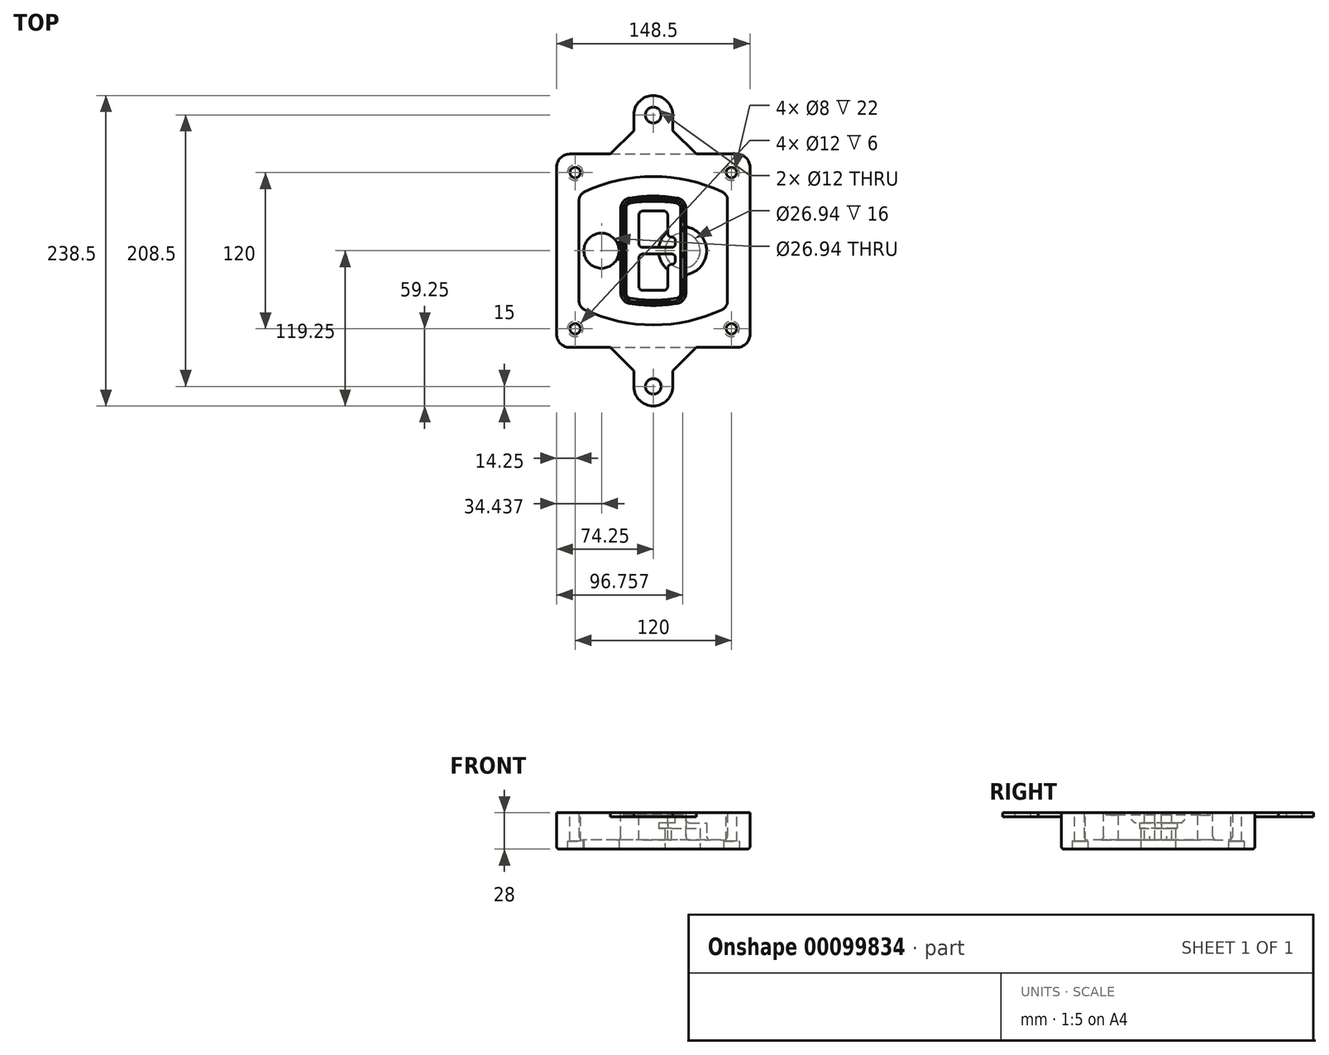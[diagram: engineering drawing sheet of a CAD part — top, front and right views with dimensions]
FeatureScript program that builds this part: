
annotation { "Feature Type Name" : "Feature", "Feature Type Description" : "" }
export const myFeature = defineFeature(function(context is Context, id is Id, definition is map)
    precondition{}
    {
        {
            var Q0;
            Q0=qCreatedBy(makeId("Top.planeOp"),FACE);
            var sketch = newSketch(context, id + "F0", { "sketchPlane" : qUnion([Q0])});
            skPoint(sketch, "E0.rect.middle", {"position": v(0, 0) * mm});
            skLineSegment(sketch, "E1.bottom", {"start": v(-64.25, -74.25) * mm, "end": v(64.25, -74.25) * mm});
            skLineSegment(sketch, "E1.top", {"start": v(-64.25, 74.25) * mm, "end": v(64.25, 74.25) * mm});
            skLineSegment(sketch, "E1.left", {"start": v(-74.25, -64.25) * mm, "end": v(-74.25, 64.25) * mm});
            skLineSegment(sketch, "E1.right", {"start": v(74.25, -64.25) * mm, "end": v(74.25, 64.25) * mm});
            skLineSegment(sketch, "E2", {"start": v(-74.25, 74.25) * mm, "end": v(74.25, -74.25) * mm, "construction": true});
            skLineSegment(sketch, "E3", {"start": v(74.25, 74.25) * mm, "end": v(-74.25, -74.25) * mm, "construction": true});
            skCircle(sketch, "E4", {"center": v(-60, 60) * mm, "radius": 4 * mm});
            skCircle(sketch, "E5", {"center": v(60, 60) * mm, "radius": 4 * mm});
            skCircle(sketch, "E6", {"center": v(60, -60) * mm, "radius": 4 * mm});
            skCircle(sketch, "E7", {"center": v(-60, -60) * mm, "radius": 4 * mm});
            skLineSegment(sketch, "E8", {"start": v(-60, 60) * mm, "end": v(60, 60) * mm, "construction": true});
            skLineSegment(sketch, "E9", {"start": v(60, 60) * mm, "end": v(60, -60) * mm, "construction": true});
            skLineSegment(sketch, "E10", {"start": v(60, -60) * mm, "end": v(-60, -60) * mm, "construction": true});
            skLineSegment(sketch, "E11", {"start": v(-60, -60) * mm, "end": v(-60, 60) * mm, "construction": true});
            skLineSegment(sketch, "E12", {"start": v(-60, 38.83) * mm, "end": v(-60, -38.83) * mm});
            skLineSegment(sketch, "E13", {"start": v(60, 38.83) * mm, "end": v(60, -38.83) * mm});
            skArc(sketch, "E14", {"start": v(54.26, 47.88) * mm, "mid": v(0, 60) * mm, "end": v(-54.26, 47.88) * mm});
            skArc(sketch, "E15", {"start": v(-54.26, -47.88) * mm, "mid": v(0, -60) * mm, "end": v(54.26, -47.88) * mm});
            skLineSegment(sketch, "E16", {"start": v(-60, 0) * mm, "end": v(60, 0) * mm, "construction": true});
            skPoint(sketch, "E17.visualSharp", {"position": v(-60, -45) * mm});
            skArc(sketch, "E17.filletArc", {"start": v(-60, -38.83) * mm, "mid": v(-58.44, -44.2) * mm, "end": v(-54.26, -47.88) * mm});
            skPoint(sketch, "E18.visualSharp", {"position": v(-60, 45) * mm});
            skArc(sketch, "E18.filletArc", {"start": v(-54.26, 47.88) * mm, "mid": v(-58.44, 44.2) * mm, "end": v(-60, 38.83) * mm});
            skPoint(sketch, "E19.visualSharp", {"position": v(60, 45) * mm});
            skArc(sketch, "E19.filletArc", {"start": v(60, 38.83) * mm, "mid": v(58.44, 44.2) * mm, "end": v(54.26, 47.88) * mm});
            skPoint(sketch, "E20.visualSharp", {"position": v(60, -45) * mm});
            skArc(sketch, "E20.filletArc", {"start": v(54.26, -47.88) * mm, "mid": v(58.44, -44.2) * mm, "end": v(60, -38.83) * mm});
            skPoint(sketch, "E21.visualSharp", {"position": v(-74.25, 74.25) * mm});
            skArc(sketch, "E21.filletArc", {"start": v(-64.25, 74.25) * mm, "mid": v(-71.32, 71.32) * mm, "end": v(-74.25, 64.25) * mm});
            skPoint(sketch, "E22.visualSharp", {"position": v(74.25, 74.25) * mm});
            skArc(sketch, "E22.filletArc", {"start": v(74.25, 64.25) * mm, "mid": v(71.32, 71.32) * mm, "end": v(64.25, 74.25) * mm});
            skPoint(sketch, "E23.visualSharp", {"position": v(74.25, -74.25) * mm});
            skArc(sketch, "E23.filletArc", {"start": v(64.25, -74.25) * mm, "mid": v(71.32, -71.32) * mm, "end": v(74.25, -64.25) * mm});
            skPoint(sketch, "E24.visualSharp", {"position": v(-74.25, -74.25) * mm});
            skArc(sketch, "E24.filletArc", {"start": v(-74.25, -64.25) * mm, "mid": v(-71.32, -71.32) * mm, "end": v(-64.25, -74.25) * mm});
            skArc(sketch, "E25.0", {"start": v(57, 38.83) * mm, "mid": v(55.9, 42.58) * mm, "end": v(52.98, 45.17) * mm});
            skLineSegment(sketch, "E25.1", {"start": v(57, 38.83) * mm, "end": v(57, -38.83) * mm});
            skArc(sketch, "E25.2", {"start": v(52.98, -45.17) * mm, "mid": v(55.9, -42.58) * mm, "end": v(57, -38.83) * mm});
            skArc(sketch, "E25.3", {"start": v(-52.98, -45.17) * mm, "mid": v(0, -57) * mm, "end": v(52.98, -45.17) * mm});
            skArc(sketch, "E25.4", {"start": v(-57, -38.83) * mm, "mid": v(-55.9, -42.58) * mm, "end": v(-52.98, -45.17) * mm});
            skArc(sketch, "E25.5", {"start": v(52.98, 45.17) * mm, "mid": v(0, 57) * mm, "end": v(-52.98, 45.17) * mm});
            skLineSegment(sketch, "E25.6", {"start": v(-57, 38.83) * mm, "end": v(-57, -38.83) * mm});
            skArc(sketch, "E25.7", {"start": v(-52.98, 45.17) * mm, "mid": v(-55.9, 42.58) * mm, "end": v(-57, 38.83) * mm});
            skArc(sketch, "E26.0", {"start": v(-55.96, 51.5) * mm, "mid": v(-61.82, 46.33) * mm, "end": v(-64, 38.83) * mm});
            skArc(sketch, "E26.1", {"start": v(55.96, 51.5) * mm, "mid": v(0, 64) * mm, "end": v(-55.96, 51.5) * mm});
            skArc(sketch, "E26.2", {"start": v(64, 38.83) * mm, "mid": v(61.82, 46.33) * mm, "end": v(55.96, 51.5) * mm});
            skLineSegment(sketch, "E26.3", {"start": v(64, 38.83) * mm, "end": v(64, -38.83) * mm});
            skArc(sketch, "E26.4", {"start": v(55.96, -51.5) * mm, "mid": v(61.82, -46.33) * mm, "end": v(64, -38.83) * mm});
            skLineSegment(sketch, "E26.5", {"start": v(-64, 38.83) * mm, "end": v(-64, -38.83) * mm});
            skArc(sketch, "E26.6", {"start": v(-55.96, -51.5) * mm, "mid": v(0, -64) * mm, "end": v(55.96, -51.5) * mm});
            skArc(sketch, "E26.7", {"start": v(-64, -38.83) * mm, "mid": v(-61.82, -46.33) * mm, "end": v(-55.96, -51.5) * mm});
            skSolve(sketch);
        }
        {
            var Q0;
            Q0=makeQuery(id+"F0.imprint","IMPRINT",FACE,{"disambiguationData":[TD([[makeQuery(id+"F0.imprint","IMPRINT",EDGE,{"derivedFrom":sQuery(id+"F0.wireOp",EDGE,"E1.bottom")}),1.0]])]});
            var Q1;
            Q1=makeQuery(id+"F0.imprint","IMPRINT",FACE,{"disambiguationData":[TD([[makeQuery(id+"F0.imprint","IMPRINT",EDGE,{"derivedFrom":sQuery(id+"F0.wireOp",EDGE,"E12")}),1.0]])]});
            var Q2;
            Q2=makeQuery(id+"F0.imprint","IMPRINT",FACE,{"disambiguationData":[TD([[makeQuery(id+"F0.imprint","IMPRINT",EDGE,{"derivedFrom":sQuery(id+"F0.wireOp",EDGE,"E25.0")}),1.0]])]});
            var Q3;
            Q3=makeQuery(id+"F0.imprint","IMPRINT",FACE,{"disambiguationData":[TD([[makeQuery(id+"F0.imprint","IMPRINT",EDGE,{"derivedFrom":sQuery(id+"F0.wireOp",EDGE,"E12")}),-1.0]])]});
            extrude(context, id + "F1", {"entities" : qUnion([Q0, Q1, Q2, Q3]), "oppositeDirection" : true, "depth" : 25 * mm});
        }
        {
            var Q0;
            Q0=makeQuery(id+"F0.imprint","IMPRINT",FACE,{"disambiguationData":[TD([[makeQuery(id+"F0.imprint","IMPRINT",EDGE,{"derivedFrom":sQuery(id+"F0.wireOp",EDGE,"E12")}),1.0]])]});
            extrude(context, id + "F2", {"entities" : qUnion([Q0]), "operationType" : NewBodyOperationType.ADD, "depth" : 3 * mm});
        }
        {
            var Q0;
            Q0=makeQuery(id+"F0.imprint","IMPRINT",FACE,{"disambiguationData":[TD([[makeQuery(id+"F0.imprint","IMPRINT",EDGE,{"derivedFrom":sQuery(id+"F0.wireOp",EDGE,"E25.0")}),1.0]])]});
            extrude(context, id + "F3", {"entities" : qUnion([Q0]), "operationType" : NewBodyOperationType.REMOVE, "oppositeDirection" : true, "depth" : 18 * mm});
        }
        {
            var Q0;
            Q0=makeQuery(id+"F2.opExtrude","CAP_FACE",FACE,{"disambiguationData":[OSD([sQuery(id+"F0.wireOp",EDGE,"E12"),sQuery(id+"F0.wireOp",EDGE,"E13"),sQuery(id+"F0.wireOp",EDGE,"E14"),sQuery(id+"F0.wireOp",EDGE,"E15"),sQuery(id+"F0.wireOp",EDGE,"E17.filletArc"),sQuery(id+"F0.wireOp",EDGE,"E18.filletArc"),sQuery(id+"F0.wireOp",EDGE,"E19.filletArc"),sQuery(id+"F0.wireOp",EDGE,"E20.filletArc"),sQuery(id+"F0.wireOp",EDGE,"E25.0"),sQuery(id+"F0.wireOp",EDGE,"E25.1"),sQuery(id+"F0.wireOp",EDGE,"E25.2"),sQuery(id+"F0.wireOp",EDGE,"E25.3"),sQuery(id+"F0.wireOp",EDGE,"E25.4"),sQuery(id+"F0.wireOp",EDGE,"E25.5"),sQuery(id+"F0.wireOp",EDGE,"E25.6"),sQuery(id+"F0.wireOp",EDGE,"E25.7")])],"isStart":false});
            var sketch = newSketch(context, id + "F4", { "sketchPlane" : qUnion([Q0])});
            skArc(sketch, "E27.0", {"start": v(-18.34, -40.45) * mm, "mid": v(0, -42) * mm, "end": v(18.34, -40.45) * mm});
            skArc(sketch, "E28.0", {"start": v(18.34, 40.45) * mm, "mid": v(0, 42) * mm, "end": v(-18.34, 40.45) * mm});
            skLineSegment(sketch, "E29", {"start": v(-25, 32.57) * mm, "end": v(-25, -32.57) * mm});
            skLineSegment(sketch, "E30", {"start": v(25, 32.57) * mm, "end": v(25, -32.57) * mm});
            skLineSegment(sketch, "E31", {"start": v(-25, 39.1) * mm, "end": v(25, 39.1) * mm, "construction": true});
            skLineSegment(sketch, "E32", {"start": v(-25, -39.1) * mm, "end": v(25, -39.1) * mm, "construction": true});
            skPoint(sketch, "E33.visualSharp", {"position": v(-25, 39.1) * mm});
            skArc(sketch, "E33.filletArc", {"start": v(-18.34, 40.45) * mm, "mid": v(-23.11, 37.73) * mm, "end": v(-25, 32.57) * mm});
            skPoint(sketch, "E34.visualSharp", {"position": v(25, 39.1) * mm});
            skArc(sketch, "E34.filletArc", {"start": v(25, 32.57) * mm, "mid": v(23.11, 37.73) * mm, "end": v(18.34, 40.45) * mm});
            skPoint(sketch, "E35.visualSharp", {"position": v(25, -39.1) * mm});
            skArc(sketch, "E35.filletArc", {"start": v(18.34, -40.45) * mm, "mid": v(23.11, -37.73) * mm, "end": v(25, -32.57) * mm});
            skPoint(sketch, "E36.visualSharp", {"position": v(-25, -39.1) * mm});
            skArc(sketch, "E36.filletArc", {"start": v(-25, -32.57) * mm, "mid": v(-23.11, -37.73) * mm, "end": v(-18.34, -40.45) * mm});
            skArc(sketch, "E37.0", {"start": v(52.98, 45.17) * mm, "mid": v(0, 57) * mm, "end": v(-52.98, 45.17) * mm});
            skArc(sketch, "E37.1", {"start": v(-52.98, 45.17) * mm, "mid": v(-55.9, 42.58) * mm, "end": v(-57, 38.83) * mm});
            skLineSegment(sketch, "E37.2", {"start": v(-57, 38.83) * mm, "end": v(-57, -38.83) * mm});
            skArc(sketch, "E37.3", {"start": v(-57, -38.83) * mm, "mid": v(-55.9, -42.58) * mm, "end": v(-52.98, -45.17) * mm});
            skArc(sketch, "E37.4", {"start": v(-52.98, -45.17) * mm, "mid": v(0, -57) * mm, "end": v(52.98, -45.17) * mm});
            skArc(sketch, "E37.5", {"start": v(52.98, -45.17) * mm, "mid": v(55.9, -42.58) * mm, "end": v(57, -38.83) * mm});
            skLineSegment(sketch, "E37.6", {"start": v(57, 38.83) * mm, "end": v(57, -38.83) * mm});
            skArc(sketch, "E37.7", {"start": v(57, 38.83) * mm, "mid": v(55.9, 42.58) * mm, "end": v(52.98, 45.17) * mm});
            skLineSegment(sketch, "E38.0", {"start": v(23, 32.57) * mm, "end": v(23, -32.57) * mm});
            skArc(sketch, "E38.1", {"start": v(18, -38.48) * mm, "mid": v(21.58, -36.44) * mm, "end": v(23, -32.57) * mm});
            skArc(sketch, "E38.2", {"start": v(-18, -38.48) * mm, "mid": v(0, -40) * mm, "end": v(18, -38.48) * mm});
            skArc(sketch, "E38.3", {"start": v(-23, -32.57) * mm, "mid": v(-21.58, -36.44) * mm, "end": v(-18, -38.48) * mm});
            skLineSegment(sketch, "E38.4", {"start": v(-23, 32.57) * mm, "end": v(-23, -32.57) * mm});
            skArc(sketch, "E38.5", {"start": v(23, 32.57) * mm, "mid": v(21.58, 36.44) * mm, "end": v(18, 38.48) * mm});
            skArc(sketch, "E38.6", {"start": v(-18, 38.48) * mm, "mid": v(-21.58, 36.44) * mm, "end": v(-23, 32.57) * mm});
            skArc(sketch, "E38.7", {"start": v(18, 38.48) * mm, "mid": v(0, 40) * mm, "end": v(-18, 38.48) * mm});
            skArc(sketch, "E39.0", {"start": v(21, 32.57) * mm, "mid": v(20.06, 35.15) * mm, "end": v(17.67, 36.5) * mm});
            skLineSegment(sketch, "E39.1", {"start": v(21, 32.57) * mm, "end": v(21, -32.57) * mm});
            skArc(sketch, "E39.2", {"start": v(17.67, -36.5) * mm, "mid": v(20.06, -35.15) * mm, "end": v(21, -32.57) * mm});
            skArc(sketch, "E39.3", {"start": v(-17.67, -36.5) * mm, "mid": v(0, -38) * mm, "end": v(17.67, -36.5) * mm});
            skArc(sketch, "E39.4", {"start": v(-21, -32.57) * mm, "mid": v(-20.06, -35.15) * mm, "end": v(-17.67, -36.5) * mm});
            skArc(sketch, "E39.5", {"start": v(17.67, 36.5) * mm, "mid": v(0, 38) * mm, "end": v(-17.67, 36.5) * mm});
            skLineSegment(sketch, "E39.6", {"start": v(-21, 32.57) * mm, "end": v(-21, -32.57) * mm});
            skArc(sketch, "E39.7", {"start": v(-17.67, 36.5) * mm, "mid": v(-20.06, 35.15) * mm, "end": v(-21, 32.57) * mm});
            skLineSegment(sketch, "E40", {"start": v(-25, 0) * mm, "end": v(25, 0) * mm, "construction": true});
            skLineSegment(sketch, "E41", {"start": v(-11, 5.5) * mm, "end": v(-11, 27.5) * mm});
            skLineSegment(sketch, "E42", {"start": v(-8, 30.5) * mm, "end": v(8, 30.5) * mm});
            skLineSegment(sketch, "E43", {"start": v(11, 27.5) * mm, "end": v(11, 13.5) * mm});
            skLineSegment(sketch, "E44", {"start": v(14, 10.5) * mm, "end": v(14, 10.5) * mm});
            skLineSegment(sketch, "E45", {"start": v(17, 7.5) * mm, "end": v(17, 5.5) * mm});
            skLineSegment(sketch, "E46", {"start": v(14, 2.5) * mm, "end": v(-8, 2.5) * mm});
            skPoint(sketch, "E47.visualSharp", {"position": v(-11, 30.5) * mm});
            skArc(sketch, "E47.filletArc", {"start": v(-8, 30.5) * mm, "mid": v(-10.12, 29.62) * mm, "end": v(-11, 27.5) * mm});
            skPoint(sketch, "E48.visualSharp", {"position": v(11, 30.5) * mm});
            skArc(sketch, "E48.filletArc", {"start": v(11, 27.5) * mm, "mid": v(10.12, 29.62) * mm, "end": v(8, 30.5) * mm});
            skPoint(sketch, "E49.visualSharp", {"position": v(11, 10.5) * mm});
            skArc(sketch, "E49.filletArc", {"start": v(11, 13.5) * mm, "mid": v(11.88, 11.38) * mm, "end": v(14, 10.5) * mm});
            skPoint(sketch, "E50.visualSharp", {"position": v(17, 10.5) * mm});
            skArc(sketch, "E50.filletArc", {"start": v(17, 7.5) * mm, "mid": v(16.12, 9.62) * mm, "end": v(14, 10.5) * mm});
            skPoint(sketch, "E51.visualSharp", {"position": v(17, 2.5) * mm});
            skArc(sketch, "E51.filletArc", {"start": v(14, 2.5) * mm, "mid": v(16.12, 3.38) * mm, "end": v(17, 5.5) * mm});
            skPoint(sketch, "E52.visualSharp", {"position": v(-11, 2.5) * mm});
            skArc(sketch, "E52.filletArc", {"start": v(-11, 5.5) * mm, "mid": v(-10.12, 3.38) * mm, "end": v(-8, 2.5) * mm});
            skLineSegment(sketch, "E53.0.MirrorCS", {"start": v(14, -2.5) * mm, "end": v(-8, -2.5) * mm});
            skArc(sketch, "E54.0.MirrorCS", {"start": v(-11, -5.5) * mm, "mid": v(-10.12, -3.38) * mm, "end": v(-8, -2.5) * mm});
            skLineSegment(sketch, "E55.0.MirrorCS", {"start": v(-11, -5.5) * mm, "end": v(-11, -27.5) * mm});
            skArc(sketch, "E56.0.MirrorCS", {"start": v(-8, -30.5) * mm, "mid": v(-10.12, -29.62) * mm, "end": v(-11, -27.5) * mm});
            skLineSegment(sketch, "E57.0.MirrorCS", {"start": v(-8, -30.5) * mm, "end": v(8, -30.5) * mm});
            skArc(sketch, "E58.0.MirrorCS", {"start": v(11, -27.5) * mm, "mid": v(10.12, -29.62) * mm, "end": v(8, -30.5) * mm});
            skLineSegment(sketch, "E59.0.MirrorCS", {"start": v(11, -27.5) * mm, "end": v(11, -13.5) * mm});
            skArc(sketch, "E60.0.MirrorCS", {"start": v(11, -13.5) * mm, "mid": v(11.88, -11.38) * mm, "end": v(14, -10.5) * mm});
            skArc(sketch, "E61.0.MirrorCS", {"start": v(17, -7.5) * mm, "mid": v(16.12, -9.62) * mm, "end": v(14, -10.5) * mm});
            skLineSegment(sketch, "E62.0.MirrorCS", {"start": v(17, -7.5) * mm, "end": v(17, -5.5) * mm});
            skArc(sketch, "E63.0.MirrorCS", {"start": v(14, -2.5) * mm, "mid": v(16.12, -3.38) * mm, "end": v(17, -5.5) * mm});
            skSolve(sketch);
        }
        {
            var Q0;
            Q0=makeQuery(id+"F4.imprint","IMPRINT",FACE,{"disambiguationData":[TD([[makeQuery(id+"F4.imprint","IMPRINT",EDGE,{"derivedFrom":sQuery(id+"F4.wireOp",EDGE,"E27.0")}),1.0]])]});
            var Q1;
            Q1=makeQuery(id+"F4.imprint","IMPRINT",FACE,{"disambiguationData":[TD([[makeQuery(id+"F4.imprint","IMPRINT",EDGE,{"derivedFrom":sQuery(id+"F4.wireOp",EDGE,"E38.0")}),-1.0]])]});
            var Q2;
            Q2=makeQuery(id+"F4.imprint","IMPRINT",FACE,{"disambiguationData":[TD([[makeQuery(id+"F4.imprint","IMPRINT",EDGE,{"derivedFrom":sQuery(id+"F4.wireOp",EDGE,"E39.0")}),1.0]])]});
            extrude(context, id + "F5", {"entities" : qUnion([Q0, Q1, Q2]), "operationType" : NewBodyOperationType.ADD, "endBound" : BoundingType.UP_TO_NEXT, "oppositeDirection" : true, "depth" : 25 * mm});
        }
        {
            var Q0;
            Q0=makeQuery(id+"F4.imprint","IMPRINT",FACE,{"disambiguationData":[TD([[makeQuery(id+"F4.imprint","IMPRINT",EDGE,{"derivedFrom":sQuery(id+"F4.wireOp",EDGE,"E38.0")}),-1.0]])]});
            extrude(context, id + "F6", {"entities" : qUnion([Q0]), "operationType" : NewBodyOperationType.REMOVE, "oppositeDirection" : true, "depth" : 2 * mm});
        }
        {
            var Q0;
            Q0=makeQuery(id+"F1.opExtrude","CAP_FACE",FACE,{"disambiguationData":[OSD([sQuery(id+"F0.wireOp",EDGE,"E1.bottom"),sQuery(id+"F0.wireOp",EDGE,"E1.top"),sQuery(id+"F0.wireOp",EDGE,"E1.left"),sQuery(id+"F0.wireOp",EDGE,"E1.right"),sQuery(id+"F0.wireOp",EDGE,"E4"),sQuery(id+"F0.wireOp",EDGE,"E5"),sQuery(id+"F0.wireOp",EDGE,"E6"),sQuery(id+"F0.wireOp",EDGE,"E7"),sQuery(id+"F0.wireOp",EDGE,"E21.filletArc"),sQuery(id+"F0.wireOp",EDGE,"E22.filletArc"),sQuery(id+"F0.wireOp",EDGE,"E23.filletArc"),sQuery(id+"F0.wireOp",EDGE,"E24.filletArc")])],"isStart":false});
            var sketch = newSketch(context, id + "F7", { "sketchPlane" : qUnion([Q0])});
            skCircle(sketch, "E64", {"center": v(22.5, 0) * mm, "radius": 13.47 * mm});
            skCircle(sketch, "E65", {"center": v(-39.81, 0) * mm, "radius": 13.47 * mm});
            skLineSegment(sketch, "E66", {"start": v(74.25, 0) * mm, "end": v(-74.25, 0) * mm});
            skCircle(sketch, "E67", {"center": v(22.5, 0) * mm, "radius": 18.47 * mm});
            skCircle(sketch, "E68", {"center": v(60, -60) * mm, "radius": 6 * mm});
            skCircle(sketch, "E69", {"center": v(-60, -60) * mm, "radius": 6 * mm});
            skCircle(sketch, "E70", {"center": v(-60, 60) * mm, "radius": 6 * mm});
            skCircle(sketch, "E71", {"center": v(60, 60) * mm, "radius": 6 * mm});
            skSolve(sketch);
        }
        {
            var Q0;
            {var subQ1=sQuery(id+"F7.wireOp",EDGE,"E66");var subQ4=sQuery(id+"F7.wireOp",EDGE,"E64");var subQ6=makeQuery(id+"F7.imprint","INTERSECT",VERTEX,{"disambiguationData":[OD(0.0)],"derivedFrom":[subQ4,subQ1]});Q0=makeQuery(id+"F7.imprint","IMPRINT",FACE,{"disambiguationData":[TD([[makeQuery(id+"F7.imprint","IMPRINT",EDGE,{"disambiguationData":[TD([[subQ6,-1.0]])],"derivedFrom":subQ4}),-1.0]])]});}
            var Q1;
            {var subQ0=sQuery(id+"F7.wireOp",EDGE,"E66");var subQ1=sQuery(id+"F7.wireOp",EDGE,"E64");var subQ3=makeQuery(id+"F7.imprint","INTERSECT",VERTEX,{"disambiguationData":[OD(0.0)],"derivedFrom":[subQ1,subQ0]});Q1=makeQuery(id+"F7.imprint","IMPRINT",FACE,{"disambiguationData":[TD([[makeQuery(id+"F7.imprint","IMPRINT",EDGE,{"disambiguationData":[TD([[subQ3,-1.0]])],"derivedFrom":subQ1}),1.0]])]});}
            var Q2;
            {var subQ0=sQuery(id+"F7.wireOp",EDGE,"E66");var subQ1=sQuery(id+"F7.wireOp",EDGE,"E64");var subQ3=makeQuery(id+"F7.imprint","INTERSECT",VERTEX,{"disambiguationData":[OD(0.0)],"derivedFrom":[subQ1,subQ0]});Q2=makeQuery(id+"F7.imprint","IMPRINT",FACE,{"disambiguationData":[TD([[makeQuery(id+"F7.imprint","IMPRINT",EDGE,{"disambiguationData":[TD([[subQ3,1.0]])],"derivedFrom":subQ1}),1.0]])]});}
            var Q3;
            {var subQ1=sQuery(id+"F7.wireOp",EDGE,"E66");var subQ4=sQuery(id+"F7.wireOp",EDGE,"E64");var subQ6=makeQuery(id+"F7.imprint","INTERSECT",VERTEX,{"disambiguationData":[OD(0.0)],"derivedFrom":[subQ4,subQ1]});Q3=makeQuery(id+"F7.imprint","IMPRINT",FACE,{"disambiguationData":[TD([[makeQuery(id+"F7.imprint","IMPRINT",EDGE,{"disambiguationData":[TD([[subQ6,1.0]])],"derivedFrom":subQ4}),-1.0]])]});}
            extrude(context, id + "F8", {"entities" : qUnion([Q0, Q1, Q2, Q3]), "operationType" : NewBodyOperationType.ADD, "oppositeDirection" : true, "depth" : 20 * mm});
        }
        {
            var Q0;
            {var subQ0=sQuery(id+"F7.wireOp",EDGE,"E66");var subQ1=sQuery(id+"F7.wireOp",EDGE,"E64");var subQ3=makeQuery(id+"F7.imprint","INTERSECT",VERTEX,{"disambiguationData":[OD(0.0)],"derivedFrom":[subQ1,subQ0]});Q0=makeQuery(id+"F7.imprint","IMPRINT",FACE,{"disambiguationData":[TD([[makeQuery(id+"F7.imprint","IMPRINT",EDGE,{"disambiguationData":[TD([[subQ3,-1.0]])],"derivedFrom":subQ1}),1.0]])]});}
            var Q1;
            {var subQ0=sQuery(id+"F7.wireOp",EDGE,"E66");var subQ1=sQuery(id+"F7.wireOp",EDGE,"E64");var subQ3=makeQuery(id+"F7.imprint","INTERSECT",VERTEX,{"disambiguationData":[OD(0.0)],"derivedFrom":[subQ1,subQ0]});Q1=makeQuery(id+"F7.imprint","IMPRINT",FACE,{"disambiguationData":[TD([[makeQuery(id+"F7.imprint","IMPRINT",EDGE,{"disambiguationData":[TD([[subQ3,1.0]])],"derivedFrom":subQ1}),1.0]])]});}
            extrude(context, id + "F9", {"entities" : qUnion([Q0, Q1]), "operationType" : NewBodyOperationType.REMOVE, "oppositeDirection" : true, "depth" : 16 * mm});
        }
        {
            var Q0;
            {var subQ0=sQuery(id+"F7.wireOp",EDGE,"E66");var subQ1=sQuery(id+"F7.wireOp",EDGE,"E65");var subQ3=makeQuery(id+"F7.imprint","INTERSECT",VERTEX,{"disambiguationData":[OD(0.0)],"derivedFrom":[subQ1,subQ0]});Q0=makeQuery(id+"F7.imprint","IMPRINT",FACE,{"disambiguationData":[TD([[makeQuery(id+"F7.imprint","IMPRINT",EDGE,{"disambiguationData":[TD([[subQ3,-1.0]])],"derivedFrom":subQ1}),1.0]])]});}
            var Q1;
            {var subQ0=sQuery(id+"F7.wireOp",EDGE,"E66");var subQ1=sQuery(id+"F7.wireOp",EDGE,"E65");var subQ3=makeQuery(id+"F7.imprint","INTERSECT",VERTEX,{"disambiguationData":[OD(0.0)],"derivedFrom":[subQ1,subQ0]});Q1=makeQuery(id+"F7.imprint","IMPRINT",FACE,{"disambiguationData":[TD([[makeQuery(id+"F7.imprint","IMPRINT",EDGE,{"disambiguationData":[TD([[subQ3,1.0]])],"derivedFrom":subQ1}),1.0]])]});}
            extrude(context, id + "F10", {"entities" : qUnion([Q0, Q1]), "operationType" : NewBodyOperationType.REMOVE, "oppositeDirection" : true, "depth" : 25 * mm});
        }
        {
            var Q0;
            Q0=makeQuery(id+"F7.imprint","IMPRINT",FACE,{"disambiguationData":[TD([[makeQuery(id+"F7.imprint","IMPRINT",EDGE,{"derivedFrom":sQuery(id+"F7.wireOp",EDGE,"E68")}),1.0]])]});
            var Q1;
            Q1=makeQuery(id+"F7.imprint","IMPRINT",FACE,{"disambiguationData":[TD([[makeQuery(id+"F7.imprint","IMPRINT",EDGE,{"derivedFrom":makeQuery(id+"F1.opExtrude","CAP_EDGE",EDGE,{"disambiguationData":[OSD([sQuery(id+"F0.wireOp",EDGE,"E5")])],"isStart":false})}),-1.0]])]});
            var Q2;
            Q2=makeQuery(id+"F7.imprint","IMPRINT",FACE,{"disambiguationData":[TD([[makeQuery(id+"F7.imprint","IMPRINT",EDGE,{"derivedFrom":sQuery(id+"F7.wireOp",EDGE,"E69")}),1.0]])]});
            var Q3;
            Q3=makeQuery(id+"F7.imprint","IMPRINT",FACE,{"disambiguationData":[TD([[makeQuery(id+"F7.imprint","IMPRINT",EDGE,{"derivedFrom":makeQuery(id+"F1.opExtrude","CAP_EDGE",EDGE,{"disambiguationData":[OSD([sQuery(id+"F0.wireOp",EDGE,"E4")])],"isStart":false})}),-1.0]])]});
            var Q4;
            Q4=makeQuery(id+"F7.imprint","IMPRINT",FACE,{"disambiguationData":[TD([[makeQuery(id+"F7.imprint","IMPRINT",EDGE,{"derivedFrom":sQuery(id+"F7.wireOp",EDGE,"E70")}),1.0]])]});
            var Q5;
            Q5=makeQuery(id+"F7.imprint","IMPRINT",FACE,{"disambiguationData":[TD([[makeQuery(id+"F7.imprint","IMPRINT",EDGE,{"derivedFrom":makeQuery(id+"F1.opExtrude","CAP_EDGE",EDGE,{"disambiguationData":[OSD([sQuery(id+"F0.wireOp",EDGE,"E7")])],"isStart":false})}),-1.0]])]});
            var Q6;
            Q6=makeQuery(id+"F7.imprint","IMPRINT",FACE,{"disambiguationData":[TD([[makeQuery(id+"F7.imprint","IMPRINT",EDGE,{"derivedFrom":sQuery(id+"F7.wireOp",EDGE,"E71")}),1.0]])]});
            var Q7;
            Q7=makeQuery(id+"F7.imprint","IMPRINT",FACE,{"disambiguationData":[TD([[makeQuery(id+"F7.imprint","IMPRINT",EDGE,{"derivedFrom":makeQuery(id+"F1.opExtrude","CAP_EDGE",EDGE,{"disambiguationData":[OSD([sQuery(id+"F0.wireOp",EDGE,"E6")])],"isStart":false})}),-1.0]])]});
            extrude(context, id + "F11", {"entities" : qUnion([Q0, Q1, Q2, Q3, Q4, Q5, Q6, Q7]), "operationType" : NewBodyOperationType.REMOVE, "oppositeDirection" : true, "depth" : 6 * mm});
        }
        {
            var Q0;
            Q0=makeQuery(id+"F9.boolean.opBoolean","COPY",FACE,{"derivedFrom":makeQuery(id+"F9.opExtrude","CAP_FACE",FACE,{"disambiguationData":[OSD([sQuery(id+"F7.wireOp",EDGE,"E64")])],"isStart":false})});
            var sketch = newSketch(context, id + "F12", { "sketchPlane" : qUnion([Q0])});
            skArc(sketch, "E72.0", {"start": v(11, 14.45) * mm, "mid": v(6.45, 9.13) * mm, "end": v(4.2, 2.5) * mm});
            skArc(sketch, "E72.1", {"start": v(4.2, -2.5) * mm, "mid": v(6.45, -9.13) * mm, "end": v(11, -14.45) * mm});
            skLineSegment(sketch, "E73", {"start": v(4.2, -2.5) * mm, "end": v(14, -2.5) * mm});
            skLineSegment(sketch, "E74.0", {"start": v(14, 2.5) * mm, "end": v(4.2, 2.5) * mm});
            skArc(sketch, "E74.1", {"start": v(14, 2.5) * mm, "mid": v(16.12, 3.38) * mm, "end": v(17, 5.5) * mm});
            skLineSegment(sketch, "E74.2", {"start": v(17, 7.5) * mm, "end": v(17, 5.5) * mm});
            skArc(sketch, "E74.3", {"start": v(17, 7.5) * mm, "mid": v(16.12, 9.62) * mm, "end": v(14, 10.5) * mm});
            skArc(sketch, "E74.4", {"start": v(11, 13.5) * mm, "mid": v(11.88, 11.38) * mm, "end": v(14, 10.5) * mm});
            skLineSegment(sketch, "E74.5", {"start": v(11, 14.45) * mm, "end": v(11, 13.5) * mm});
            skLineSegment(sketch, "E74.7", {"start": v(14, -2.5) * mm, "end": v(4.2, -2.5) * mm});
            skArc(sketch, "E74.8", {"start": v(14, -2.5) * mm, "mid": v(16.12, -3.38) * mm, "end": v(17, -5.5) * mm});
            skLineSegment(sketch, "E74.9", {"start": v(17, -7.5) * mm, "end": v(17, -5.5) * mm});
            skArc(sketch, "E74.10", {"start": v(17, -7.5) * mm, "mid": v(16.12, -9.62) * mm, "end": v(14, -10.5) * mm});
            skArc(sketch, "E74.11", {"start": v(11, -13.5) * mm, "mid": v(11.88, -11.38) * mm, "end": v(14, -10.5) * mm});
            skLineSegment(sketch, "E74.12", {"start": v(11, -14.45) * mm, "end": v(11, -13.5) * mm});
            skPoint(sketch, "E75.orphan", {"position": v(11, -27.5) * mm});
            skPoint(sketch, "E76.orphan", {"position": v(-8, -2.5) * mm});
            skPoint(sketch, "E77.orphan", {"position": v(-8, 2.5) * mm});
            skPoint(sketch, "E78.orphan", {"position": v(11, 27.5) * mm});
            skSolve(sketch);
        }
        {
            var Q0;
            {var subQ7=sQuery(id+"F12.wireOp",EDGE,"E72.0");var subQ14=sQuery(id+"F12.wireOp",EDGE,"E72.1");var subQ16=sQuery(id+"F12.wireOp",EDGE,"E74.1");var subQ18=sQuery(id+"F12.wireOp",EDGE,"E74.8");Q0=qUnion([makeQuery(id+"F12.imprint","IMPRINT",FACE,{"disambiguationData":[TD([[makeQuery(id+"F12.imprint","IMPRINT",EDGE,{"derivedFrom":subQ7}),1.0]])]}),makeQuery(id+"F12.imprint","IMPRINT",FACE,{"disambiguationData":[TD([[makeQuery(id+"F12.imprint","IMPRINT",EDGE,{"derivedFrom":subQ14}),1.0]])]}),makeQuery(id+"F12.imprint","IMPRINT",FACE,{"disambiguationData":[TD([[makeQuery(id+"F12.imprint","IMPRINT",EDGE,{"derivedFrom":subQ16}),1.0]])]}),makeQuery(id+"F12.imprint","IMPRINT",FACE,{"disambiguationData":[TD([[makeQuery(id+"F12.imprint","IMPRINT",EDGE,{"derivedFrom":subQ18}),-1.0]])]})]);}
            var Q1;
            Q1=makeQuery(id+"F5.boolean.opBoolean","SPLIT",FACE,{"disambiguationData":[TD([makeQuery(id+"F5.opExtrude","SWEPT_FACE",FACE,{"disambiguationData":[OSD([sQuery(id+"F4.wireOp",EDGE,"E41")])]})])],"derivedFrom":makeQuery(id+"F3.boolean.opBoolean","COPY",FACE,{"derivedFrom":makeQuery(id+"F3.opExtrude","CAP_FACE",FACE,{"disambiguationData":[OSD([sQuery(id+"F0.wireOp",EDGE,"E25.0"),sQuery(id+"F0.wireOp",EDGE,"E25.1"),sQuery(id+"F0.wireOp",EDGE,"E25.2"),sQuery(id+"F0.wireOp",EDGE,"E25.3"),sQuery(id+"F0.wireOp",EDGE,"E25.4"),sQuery(id+"F0.wireOp",EDGE,"E25.5"),sQuery(id+"F0.wireOp",EDGE,"E25.6"),sQuery(id+"F0.wireOp",EDGE,"E25.7")])],"isStart":false})})});
            extrude(context, id + "F13", {"entities" : qUnion([Q0]), "operationType" : NewBodyOperationType.REMOVE, "endBound" : BoundingType.UP_TO_SURFACE, "endBoundEntityFace" : qUnion([Q1]), "depth" : 25 * mm});
        }
        {
            var Q0;
            Q0=makeQuery(id+"F3.boolean.opBoolean","COPY",EDGE,{"derivedFrom":makeQuery(id+"F3.opExtrude","CAP_EDGE",EDGE,{"disambiguationData":[OSD([sQuery(id+"F0.wireOp",EDGE,"E25.6")])],"isStart":false})});
            var Q1;
            Q1=makeQuery(id+"F8.boolean.opBoolean","INTERSECT",EDGE,{"derivedFrom":[makeQuery(id+"F5.opExtrude","SWEPT_FACE",FACE,{"disambiguationData":[OSD([sQuery(id+"F4.wireOp",EDGE,"E30")])]}),makeQuery(id+"F8.opExtrude","CAP_FACE",FACE,{"disambiguationData":[OSD([sQuery(id+"F7.wireOp",EDGE,"E67")])],"isStart":false})]});
            var Q2;
            Q2=makeQuery(id+"F8.boolean.opBoolean","INTERSECT",EDGE,{"disambiguationData":[OD(1.0)],"derivedFrom":[makeQuery(id+"F5.opExtrude","SWEPT_FACE",FACE,{"disambiguationData":[OSD([sQuery(id+"F4.wireOp",EDGE,"E30")])]}),makeQuery(id+"F8.opExtrude","SWEPT_FACE",FACE,{"disambiguationData":[OSD([sQuery(id+"F7.wireOp",EDGE,"E67")])]})]});
            var Q3;
            {var subQ0=sQuery(id+"F4.wireOp",EDGE,"E30");Q3=makeQuery(id+"F8.boolean.opBoolean","SPLIT",EDGE,{"disambiguationData":[TD([makeQuery(id+"F5.opExtrude","SWEPT_FACE",FACE,{"disambiguationData":[OSD([sQuery(id+"F4.wireOp",EDGE,"E35.filletArc")])]})])],"derivedFrom":makeQuery(id+"F5.opExtrude","CAP_EDGE",EDGE,{"disambiguationData":[OSD([subQ0])],"isStart":false})});}
            var Q4;
            {var subQ0=sQuery(id+"F0.wireOp",EDGE,"E25.7");var subQ1=sQuery(id+"F0.wireOp",EDGE,"E25.1");var subQ2=sQuery(id+"F0.wireOp",EDGE,"E25.6");var subQ3=sQuery(id+"F0.wireOp",EDGE,"E25.5");var subQ4=sQuery(id+"F0.wireOp",EDGE,"E25.4");var subQ5=sQuery(id+"F0.wireOp",EDGE,"E25.0");var subQ6=sQuery(id+"F0.wireOp",EDGE,"E25.2");var subQ7=sQuery(id+"F0.wireOp",EDGE,"E25.3");Q4=makeQuery(id+"F8.boolean.opBoolean","INTERSECT",EDGE,{"derivedFrom":[makeQuery(id+"F5.boolean.opBoolean","SPLIT",FACE,{"disambiguationData":[TD([makeQuery(id+"F2.opExtrude","SWEPT_FACE",FACE,{"disambiguationData":[OSD([subQ5])]})])],"derivedFrom":makeQuery(id+"F3.boolean.opBoolean","COPY",FACE,{"derivedFrom":makeQuery(id+"F3.opExtrude","CAP_FACE",FACE,{"disambiguationData":[OSD([subQ5,subQ1,subQ6,subQ7,subQ4,subQ3,subQ2,subQ0])],"isStart":false})})}),makeQuery(id+"F8.opExtrude","SWEPT_FACE",FACE,{"disambiguationData":[OSD([sQuery(id+"F7.wireOp",EDGE,"E67")])]})]});}
            var Q5;
            Q5=makeQuery(id+"F8.boolean.opBoolean","INTERSECT",EDGE,{"disambiguationData":[OD(0.0)],"derivedFrom":[makeQuery(id+"F5.opExtrude","SWEPT_FACE",FACE,{"disambiguationData":[OSD([sQuery(id+"F4.wireOp",EDGE,"E30")])]}),makeQuery(id+"F8.opExtrude","SWEPT_FACE",FACE,{"disambiguationData":[OSD([sQuery(id+"F7.wireOp",EDGE,"E67")])]})]});
            fillet(context, id + "F14", {"entities" : qUnion([Q0, Q1, Q2, Q3, Q4, Q5]), "radius" : 3 * mm, "tangentPropagation" : true, "allowEdgeOverflow" : false});
        }
        {
            var Q0;
            Q0=makeQuery(id+"F1.opExtrude","CAP_EDGE",EDGE,{"disambiguationData":[OSD([sQuery(id+"F0.wireOp",EDGE,"E1.bottom")])],"isStart":false});
            fillet(context, id + "F15", {"entities" : qUnion([Q0]), "radius" : 2 * mm, "tangentPropagation" : true, "allowEdgeOverflow" : false});
        }
        {
            var Q0;
            {var subQ0=sQuery(id+"F0.wireOp",EDGE,"E22.filletArc");var subQ1=sQuery(id+"F0.wireOp",EDGE,"E7");var subQ2=sQuery(id+"F0.wireOp",EDGE,"E6");var subQ3=sQuery(id+"F0.wireOp",EDGE,"E5");var subQ4=sQuery(id+"F0.wireOp",EDGE,"E4");var subQ5=sQuery(id+"F0.wireOp",EDGE,"E1.bottom");var subQ6=sQuery(id+"F0.wireOp",EDGE,"E21.filletArc");var subQ7=sQuery(id+"F0.wireOp",EDGE,"E1.top");var subQ8=sQuery(id+"F0.wireOp",EDGE,"E1.left");var subQ9=sQuery(id+"F0.wireOp",EDGE,"E1.right");var subQ10=sQuery(id+"F0.wireOp",EDGE,"E23.filletArc");var subQ11=sQuery(id+"F0.wireOp",EDGE,"E24.filletArc");Q0=makeQuery(id+"F2.boolean.opBoolean","SPLIT",FACE,{"disambiguationData":[TD([makeQuery(id+"F1.opExtrude","SWEPT_FACE",FACE,{"disambiguationData":[OSD([subQ5])]})])],"derivedFrom":makeQuery(id+"F1.opExtrude","CAP_FACE",FACE,{"disambiguationData":[OSD([subQ5,subQ7,subQ8,subQ9,subQ4,subQ3,subQ2,subQ1,subQ6,subQ0,subQ10,subQ11])],"isStart":true})});}
            var sketch = newSketch(context, id + "F16", { "sketchPlane" : qUnion([Q0])});
            skLineSegment(sketch, "E79", {"start": v(0, 74.25) * mm, "end": v(0, 104.25) * mm, "construction": true});
            skCircle(sketch, "E80", {"center": v(0, 104.25) * mm, "radius": 6 * mm});
            skLineSegment(sketch, "E81", {"start": v(-33, 74.25) * mm, "end": v(-15, 92.25) * mm});
            skLineSegment(sketch, "E82", {"start": v(-15, 92.25) * mm, "end": v(-15, 104.25) * mm});
            skArc(sketch, "E83", {"start": v(15, 104.25) * mm, "mid": v(0, 119.25) * mm, "end": v(-15, 104.25) * mm});
            skLineSegment(sketch, "E84", {"start": v(15, 104.25) * mm, "end": v(15, 92.25) * mm});
            skLineSegment(sketch, "E85", {"start": v(15, 92.25) * mm, "end": v(33, 74.25) * mm});
            skLineSegment(sketch, "E86", {"start": v(-74.25, 0) * mm, "end": v(74.25, 0) * mm, "construction": true});
            skLineSegment(sketch, "E87.MirrorCS", {"start": v(-33, -74.25) * mm, "end": v(-15, -92.25) * mm});
            skLineSegment(sketch, "E88.MirrorCS", {"start": v(-15, -92.25) * mm, "end": v(-15, -104.25) * mm});
            skArc(sketch, "E89.MirrorCS", {"start": v(15, -104.25) * mm, "mid": v(0, -119.25) * mm, "end": v(-15, -104.25) * mm});
            skCircle(sketch, "E90.MirrorC", {"center": v(0, -104.25) * mm, "radius": 6 * mm});
            skLineSegment(sketch, "E91.MirrorCS", {"start": v(0, -74.25) * mm, "end": v(0, -104.25) * mm, "construction": true});
            skLineSegment(sketch, "E92.MirrorCS", {"start": v(15, -104.25) * mm, "end": v(15, -92.25) * mm});
            skLineSegment(sketch, "E93.MirrorCS", {"start": v(15, -92.25) * mm, "end": v(33, -74.25) * mm});
            skSolve(sketch);
        }
        {
            var Q0;
            {var subQ0=sQuery(id+"F16.wireOp",EDGE,"E87.MirrorCS");Q0=makeQuery(id+"F16.imprint","IMPRINT",FACE,{"disambiguationData":[TD([[makeQuery(id+"F16.imprint","IMPRINT",EDGE,{"derivedFrom":subQ0}),1.0]])]});}
            var Q1;
            Q1=makeQuery(id+"F16.imprint","IMPRINT",FACE,{"disambiguationData":[TD([[makeQuery(id+"F16.imprint","IMPRINT",EDGE,{"derivedFrom":makeQuery(id+"F1.opExtrude","CAP_EDGE",EDGE,{"disambiguationData":[OSD([sQuery(id+"F0.wireOp",EDGE,"E1.left")])],"isStart":true})}),-1.0]])]});
            var Q2;
            Q2=makeQuery(id+"F16.imprint","IMPRINT",FACE,{"disambiguationData":[TD([[makeQuery(id+"F16.imprint","IMPRINT",EDGE,{"derivedFrom":sQuery(id+"F16.wireOp",EDGE,"E80")}),-1.0]])]});
            var Q3;
            Q3=makeQuery(id+"F2.opExtrude","CAP_FACE",FACE,{"disambiguationData":[OSD([sQuery(id+"F0.wireOp",EDGE,"E12"),sQuery(id+"F0.wireOp",EDGE,"E13"),sQuery(id+"F0.wireOp",EDGE,"E14"),sQuery(id+"F0.wireOp",EDGE,"E15"),sQuery(id+"F0.wireOp",EDGE,"E17.filletArc"),sQuery(id+"F0.wireOp",EDGE,"E18.filletArc"),sQuery(id+"F0.wireOp",EDGE,"E19.filletArc"),sQuery(id+"F0.wireOp",EDGE,"E20.filletArc"),sQuery(id+"F0.wireOp",EDGE,"E25.0"),sQuery(id+"F0.wireOp",EDGE,"E25.1"),sQuery(id+"F0.wireOp",EDGE,"E25.2"),sQuery(id+"F0.wireOp",EDGE,"E25.3"),sQuery(id+"F0.wireOp",EDGE,"E25.4"),sQuery(id+"F0.wireOp",EDGE,"E25.5"),sQuery(id+"F0.wireOp",EDGE,"E25.6"),sQuery(id+"F0.wireOp",EDGE,"E25.7")])],"isStart":false});
            extrude(context, id + "F17", {"entities" : qUnion([Q0, Q1, Q2]), "operationType" : NewBodyOperationType.ADD, "endBound" : BoundingType.UP_TO_SURFACE, "endBoundEntityFace" : qUnion([Q3]), "depth" : 25 * mm});
        }
    });
